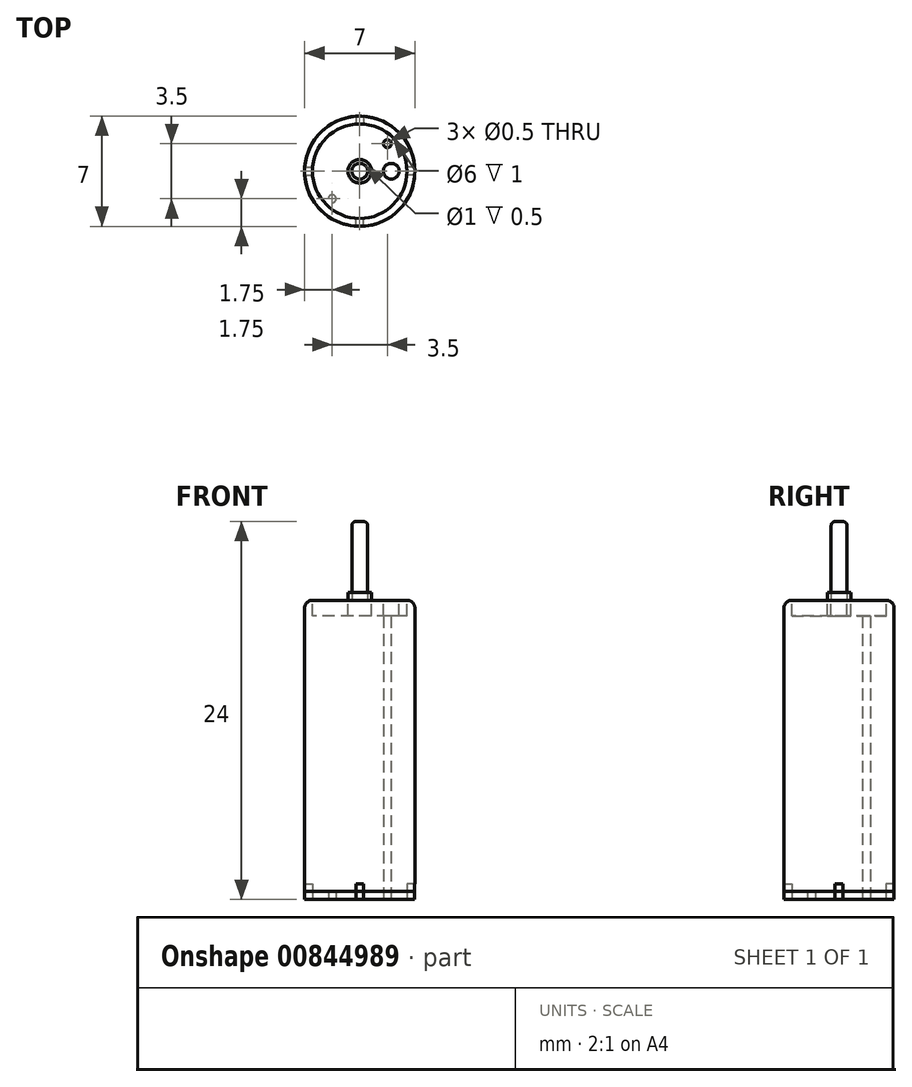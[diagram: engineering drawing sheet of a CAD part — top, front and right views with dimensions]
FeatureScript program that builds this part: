
annotation { "Feature Type Name" : "Feature", "Feature Type Description" : "" }
export const myFeature = defineFeature(function(context is Context, id is Id, definition is map)
    precondition{}
    {
        {
            var Q0;
            Q0=qCreatedBy(makeId("Top.planeOp"),FACE);
            var sketch = newSketch(context, id + "F0", { "sketchPlane" : qUnion([Q0])});
            skLineSegment(sketch, "E0.top", {"start": v(-0.25, 3) * mm, "end": v(0.25, 3) * mm});
            skLineSegment(sketch, "E0.left", {"start": v(-0.25, 3.5) * mm, "end": v(-0.25, 3) * mm});
            skLineSegment(sketch, "E0.right", {"start": v(0.25, 3.5) * mm, "end": v(0.25, 3) * mm});
            skLineSegment(sketch, "E1.1.0", {"start": v(-3, -0.25) * mm, "end": v(-3, 0.25) * mm});
            skLineSegment(sketch, "E1.1.1", {"start": v(-3.5, 0.25) * mm, "end": v(-3, 0.25) * mm});
            skLineSegment(sketch, "E1.1.2", {"start": v(-3.5, -0.25) * mm, "end": v(-3, -0.25) * mm});
            skLineSegment(sketch, "E1.2.0", {"start": v(0.25, -3) * mm, "end": v(-0.25, -3) * mm});
            skLineSegment(sketch, "E1.2.1", {"start": v(-0.25, -3.5) * mm, "end": v(-0.25, -3) * mm});
            skLineSegment(sketch, "E1.2.2", {"start": v(0.25, -3.5) * mm, "end": v(0.25, -3) * mm});
            skLineSegment(sketch, "E1.3.0", {"start": v(3, 0.25) * mm, "end": v(3, -0.25) * mm});
            skLineSegment(sketch, "E1.3.1", {"start": v(3.5, -0.25) * mm, "end": v(3, -0.25) * mm});
            skLineSegment(sketch, "E1.3.2", {"start": v(3.5, 0.25) * mm, "end": v(3, 0.25) * mm});
            skPoint(sketch, "E1.center", {"position": v(0, 0) * mm});
            skCircle(sketch, "E2", {"center": v(-1.75, -1.75) * mm, "radius": 0.25 * mm});
            skLineSegment(sketch, "E3", {"start": v(-1.57, 1.57) * mm, "end": v(2.01, -2.01) * mm, "construction": true});
            skCircle(sketch, "E4.MirrorC", {"center": v(1.75, 1.75) * mm, "radius": 0.25 * mm});
            skCircle(sketch, "E5.converted", {"center": v(0, 0) * mm, "radius": 3.5 * mm});
            skSolve(sketch);
        }
        {
            var Q0;
            Q0=makeQuery(id+"F0.imprint","IMPRINT",FACE,{"disambiguationData":[TD([[makeQuery(id+"F0.imprint","IMPRINT",EDGE,{"derivedFrom":sQuery(id+"F0.wireOp",EDGE,"E0.top")}),-1.0]])]});
            extrude(context, id + "F1", {"entities" : qUnion([Q0]), "depth" : .5 * mm});
        }
        {
            var Q0;
            Q0=makeQuery(id+"F0.imprint","IMPRINT",FACE,{"disambiguationData":[TD([[makeQuery(id+"F0.imprint","IMPRINT",EDGE,{"derivedFrom":sQuery(id+"F0.wireOp",EDGE,"E0.top")}),-1.0]])]});
            var Q1;
            Q1=makeQuery(id+"F0.imprint","IMPRINT",FACE,{"disambiguationData":[TD([[makeQuery(id+"F0.imprint","IMPRINT",EDGE,{"derivedFrom":sQuery(id+"F0.wireOp",EDGE,"E2")}),1.0]])]});
            var Q2;
            Q2=makeQuery(id+"F0.imprint","IMPRINT",FACE,{"disambiguationData":[TD([[makeQuery(id+"F0.imprint","IMPRINT",EDGE,{"derivedFrom":sQuery(id+"F0.wireOp",EDGE,"E4.MirrorC")}),-1.0]])]});
            extrude(context, id + "F2", {"entities" : qUnion([Q0, Q1, Q2]), "depth" : 1 * mm, "hasSecondDirection" : true, "secondDirectionOppositeDirection" : false, "secondDirectionDepth" : .5 * mm});
        }
        {
            var Q0;
            Q0=makeQuery(id+"F0.imprint","IMPRINT",FACE,{"disambiguationData":[TD([[makeQuery(id+"F0.imprint","IMPRINT",EDGE,{"derivedFrom":sQuery(id+"F0.wireOp",EDGE,"E0.top")}),-1.0]])]});
            var Q1;
            Q1=makeQuery(id+"F0.imprint","IMPRINT",FACE,{"disambiguationData":[TD([[makeQuery(id+"F0.imprint","IMPRINT",EDGE,{"derivedFrom":sQuery(id+"F0.wireOp",EDGE,"E1.2.0")}),1.0]])]});
            var Q2;
            Q2=makeQuery(id+"F0.imprint","IMPRINT",FACE,{"disambiguationData":[TD([[makeQuery(id+"F0.imprint","IMPRINT",EDGE,{"derivedFrom":sQuery(id+"F0.wireOp",EDGE,"E1.1.0")}),1.0]])]});
            var Q3;
            Q3=makeQuery(id+"F0.imprint","IMPRINT",FACE,{"disambiguationData":[TD([[makeQuery(id+"F0.imprint","IMPRINT",EDGE,{"derivedFrom":sQuery(id+"F0.wireOp",EDGE,"E0.top")}),1.0]])]});
            var Q4;
            Q4=makeQuery(id+"F0.imprint","IMPRINT",FACE,{"disambiguationData":[TD([[makeQuery(id+"F0.imprint","IMPRINT",EDGE,{"derivedFrom":sQuery(id+"F0.wireOp",EDGE,"E2")}),1.0]])]});
            var Q5;
            Q5=makeQuery(id+"F0.imprint","IMPRINT",FACE,{"disambiguationData":[TD([[makeQuery(id+"F0.imprint","IMPRINT",EDGE,{"derivedFrom":sQuery(id+"F0.wireOp",EDGE,"E4.MirrorC")}),-1.0]])]});
            var Q6;
            Q6=makeQuery(id+"F0.imprint","IMPRINT",FACE,{"disambiguationData":[TD([[makeQuery(id+"F0.imprint","IMPRINT",EDGE,{"derivedFrom":sQuery(id+"F0.wireOp",EDGE,"E1.3.0")}),1.0]])]});
            extrude(context, id + "F3", {"entities" : qUnion([Q0, Q1, Q2, Q3, Q4, Q5, Q6]), "operationType" : NewBodyOperationType.ADD, "depth" : 19 * mm, "hasSecondDirection" : true, "secondDirectionOppositeDirection" : false, "secondDirectionDepth" : 1 * mm});
        }
        {
            var Q0;
            Q0=makeQuery(id+"F3.opExtrude","CAP_EDGE",EDGE,{"disambiguationData":[OSD([sQuery(id+"F0.wireOp",EDGE,"E5.converted")])],"isStart":false});
            fillet(context, id + "F4", {"entities" : qUnion([Q0]), "radius" : .5 * mm, "tangentPropagation" : true, "allowEdgeOverflow" : false});
        }
        {
            var Q0;
            Q0=makeQuery(id+"F3.opExtrude","CAP_FACE",FACE,{"disambiguationData":[OSD([sQuery(id+"F0.wireOp",EDGE,"E5.converted")])],"isStart":false});
            var sketch = newSketch(context, id + "F5", { "sketchPlane" : qUnion([Q0])});
            skCircle(sketch, "E6", {"center": v(-2, 0) * mm, "radius": 0.5 * mm});
            skCircle(sketch, "E7.MirrorC", {"center": v(2, 0) * mm, "radius": 0.5 * mm});
            skCircle(sketch, "E8", {"center": v(0, 0) * mm, "radius": 0.75 * mm});
            skCircle(sketch, "E9", {"center": v(0, 0) * mm, "radius": 0.5 * mm});
            skSolve(sketch);
        }
        {
            var Q0;
            Q0=makeQuery(id+"F5.imprint","IMPRINT",FACE,{"disambiguationData":[TD([[makeQuery(id+"F5.imprint","IMPRINT",EDGE,{"derivedFrom":sQuery(id+"F5.wireOp",EDGE,"E6")}),1.0]])]});
            var Q1;
            Q1=makeQuery(id+"F5.imprint","IMPRINT",FACE,{"disambiguationData":[TD([[makeQuery(id+"F5.imprint","IMPRINT",EDGE,{"derivedFrom":sQuery(id+"F5.wireOp",EDGE,"E7.MirrorC")}),-1.0]])]});
            extrude(context, id + "F6", {"entities" : qUnion([Q0, Q1]), "operationType" : NewBodyOperationType.REMOVE, "oppositeDirection" : true, "depth" : 1 * mm});
        }
        {
            var Q0;
            Q0=makeQuery(id+"F5.imprint","IMPRINT",FACE,{"disambiguationData":[TD([[makeQuery(id+"F5.imprint","IMPRINT",EDGE,{"derivedFrom":sQuery(id+"F5.wireOp",EDGE,"E8")}),1.0]])]});
            extrude(context, id + "F7", {"entities" : qUnion([Q0]), "depth" : .5 * mm});
        }
        {
            var Q0;
            Q0=makeQuery(id+"F5.imprint","IMPRINT",FACE,{"disambiguationData":[TD([[makeQuery(id+"F5.imprint","IMPRINT",EDGE,{"derivedFrom":sQuery(id+"F5.wireOp",EDGE,"E9")}),1.0]])]});
            extrude(context, id + "F8", {"entities" : qUnion([Q0]), "depth" : 5 * mm});
        }
        {
            var Q0;
            Q0=makeQuery(id+"F8.opExtrude","CAP_EDGE",EDGE,{"disambiguationData":[OSD([sQuery(id+"F5.wireOp",EDGE,"E9")])],"isStart":false});
            fillet(context, id + "F9", {"entities" : qUnion([Q0]), "radius" : .25 * mm, "tangentPropagation" : true, "allowEdgeOverflow" : false});
        }
    });
